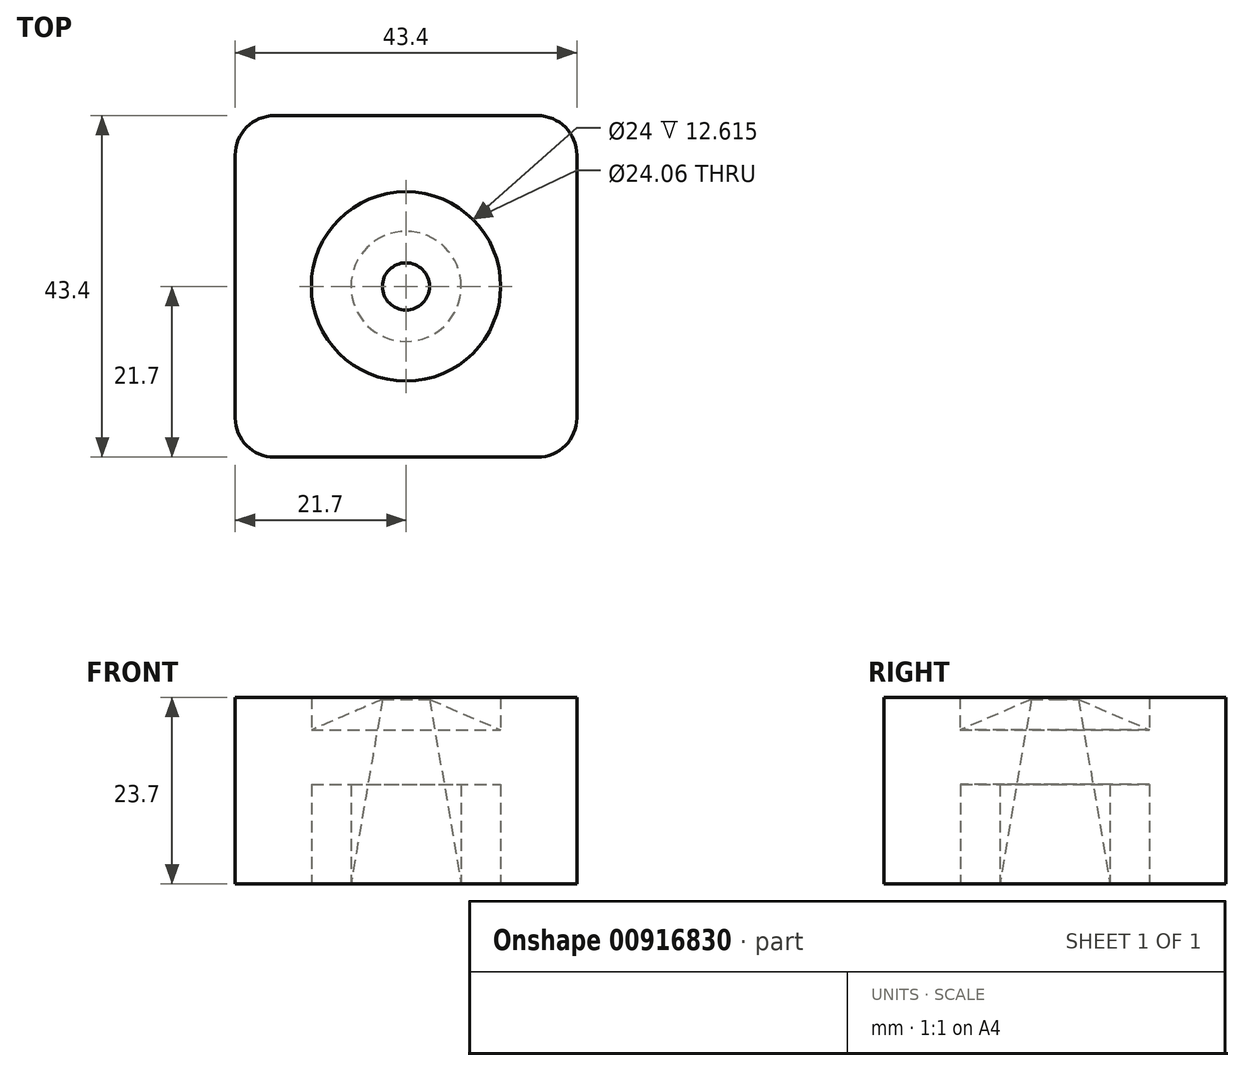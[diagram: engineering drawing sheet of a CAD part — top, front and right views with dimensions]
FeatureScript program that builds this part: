
annotation { "Feature Type Name" : "Feature", "Feature Type Description" : "" }
export const myFeature = defineFeature(function(context is Context, id is Id, definition is map)
    precondition{}
    {
        {
            var Q0;
            Q0=qCreatedBy(makeId("Front.planeOp"),FACE);
            var sketch = newSketch(context, id + "F0", { "sketchPlane" : qUnion([Q0])});
            skLineSegment(sketch, "E0", {"start": v(0, 0) * mm, "end": v(0, 40) * mm});
            skLineSegment(sketch, "E1", {"start": v(3, 23.42) * mm, "end": v(7, 0) * mm});
            skPoint(sketch, "E2", {"position": v(3, 23.42) * mm});
            skPoint(sketch, "E3", {"position": v(0, 23.42) * mm});
            skLineSegment(sketch, "E4", {"start": v(7, 0) * mm, "end": v(7, 12.61) * mm});
            skLineSegment(sketch, "E5", {"start": v(7, 12.61) * mm, "end": v(12, 12.61) * mm});
            skLineSegment(sketch, "E6", {"start": v(12, 12.61) * mm, "end": v(12, 0) * mm});
            skLineSegment(sketch, "E7", {"start": v(12, 0) * mm, "end": v(21.5, 0) * mm});
            skLineSegment(sketch, "E8", {"start": v(21.5, 0) * mm, "end": v(21.5, 15.48) * mm});
            skLineSegment(sketch, "E9", {"start": v(21.5, 15.48) * mm, "end": v(3, 23.42) * mm});
            skSolve(sketch);
        }
        {
            var Q0;
            Q0=makeQuery(id+"F0.imprint","IMPRINT",FACE,{"disambiguationData":[TD([[makeQuery(id+"F0.imprint","IMPRINT",EDGE,{"derivedFrom":sQuery(id+"F0.wireOp",EDGE,"E1")}),1.0]])]});
            var Q1;
            Q1=sQuery(id+"F0.wireOp",EDGE,"E0");
            revolve(context, id + "F1", {"surfaceOperationType" : NewSurfaceOperationType.NEW, "entities" : qUnion([Q0]), "axis" : qUnion([Q1]), "revolveType" : RevolveType.FULL});
        }
        {
            var Q0;
            Q0=qCreatedBy(makeId("Top.planeOp"),FACE);
            var sketch = newSketch(context, id + "F2", { "sketchPlane" : qUnion([Q0])});
            skCircle(sketch, "E10.cCircle", {"center": v(0, 0) * mm, "radius": 21.7 * mm, "construction": true});
            skLineSegment(sketch, "E10.0", {"start": v(-16.7, 21.7) * mm, "end": v(16.7, 21.7) * mm});
            skLineSegment(sketch, "E10.1", {"start": v(21.7, 16.7) * mm, "end": v(21.7, -16.7) * mm});
            skLineSegment(sketch, "E10.2", {"start": v(16.7, -21.7) * mm, "end": v(-16.7, -21.7) * mm});
            skLineSegment(sketch, "E10.3", {"start": v(-21.7, -16.7) * mm, "end": v(-21.7, 16.7) * mm});
            skPoint(sketch, "E10.0.midPoint", {"position": v(0, 21.7) * mm});
            skPoint(sketch, "E11.visualSharp", {"position": v(-21.7, 21.7) * mm});
            skArc(sketch, "E11.filletArc", {"start": v(-16.7, 21.7) * mm, "mid": v(-20.23, 20.23) * mm, "end": v(-21.7, 16.7) * mm});
            skPoint(sketch, "E12.visualSharp", {"position": v(-21.7, -21.7) * mm});
            skArc(sketch, "E12.filletArc", {"start": v(-21.7, -16.7) * mm, "mid": v(-20.23, -20.23) * mm, "end": v(-16.7, -21.7) * mm});
            skPoint(sketch, "E13.visualSharp", {"position": v(21.7, -21.7) * mm});
            skArc(sketch, "E13.filletArc", {"start": v(16.7, -21.7) * mm, "mid": v(20.23, -20.23) * mm, "end": v(21.7, -16.7) * mm});
            skPoint(sketch, "E14.visualSharp", {"position": v(21.7, 21.7) * mm});
            skArc(sketch, "E14.filletArc", {"start": v(21.7, 16.7) * mm, "mid": v(20.23, 20.23) * mm, "end": v(16.7, 21.7) * mm});
            skCircle(sketch, "E15", {"center": v(0, 0) * mm, "radius": 6.93 * mm});
            skCircle(sketch, "E16", {"center": v(0, 0) * mm, "radius": 12.03 * mm});
            skSolve(sketch);
        }
        {
            var Q0;
            Q0 = qSketchRegion(id + "F2", true);
            extrude(context, id + "F3", {"entities" : qUnion([Q0]), "operationType" : NewBodyOperationType.ADD, "depth" : 23.7 * mm, "offsetDistance" : 25 * mm});
        }
    });
